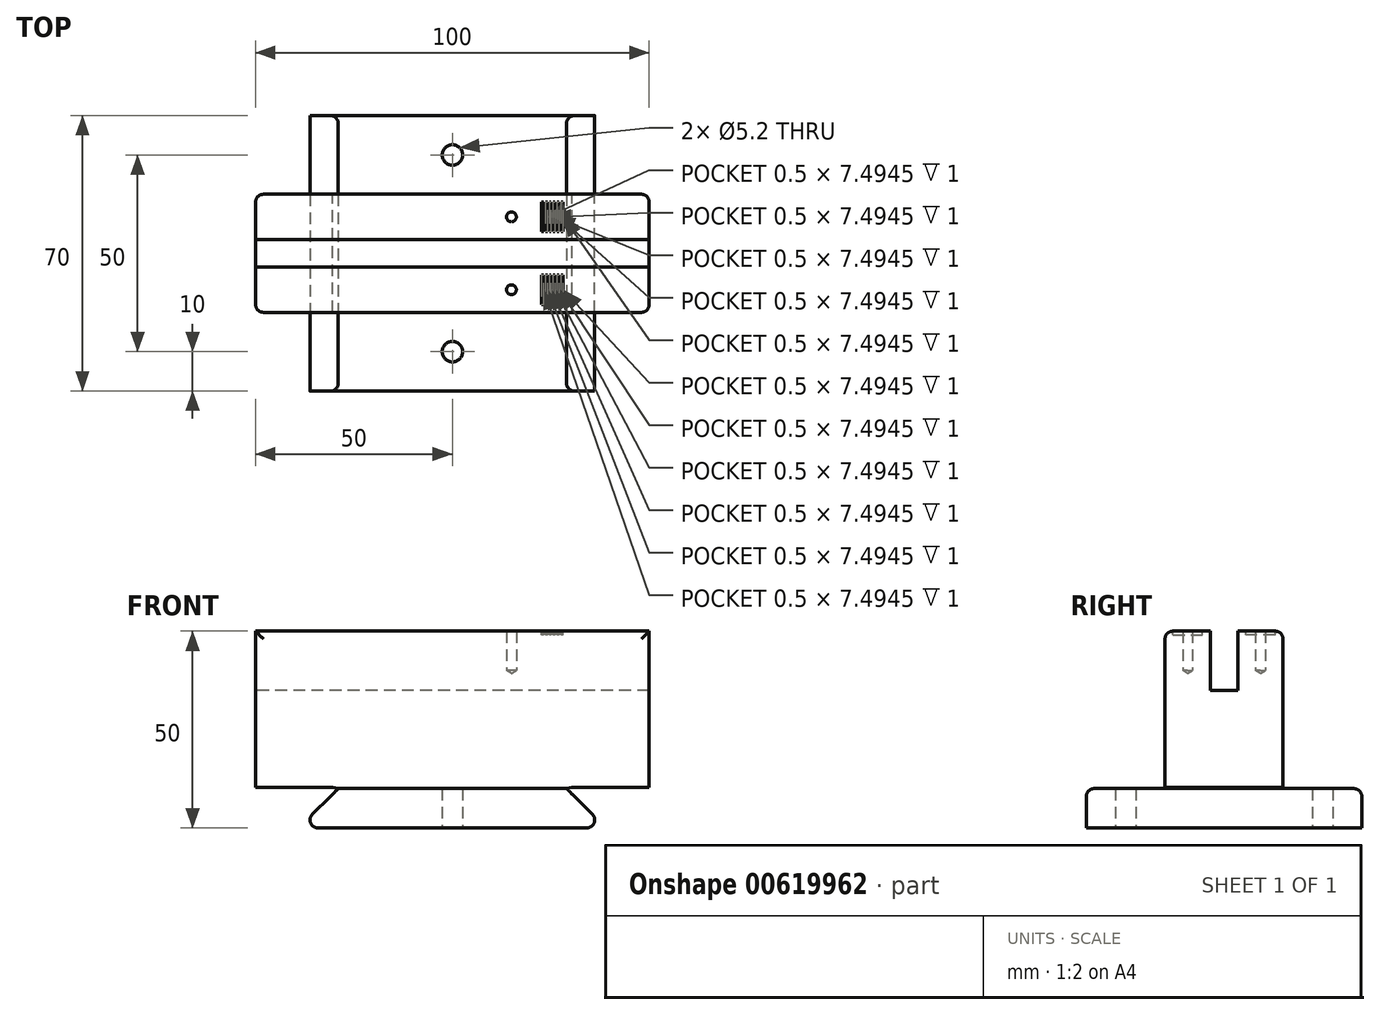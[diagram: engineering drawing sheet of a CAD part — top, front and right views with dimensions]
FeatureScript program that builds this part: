
annotation { "Feature Type Name" : "Feature", "Feature Type Description" : "" }
export const myFeature = defineFeature(function(context is Context, id is Id, definition is map)
    precondition{}
    {
        {
            var Q0;
            Q0=qCreatedBy(makeId("Top.planeOp"),FACE);
            var sketch = newSketch(context, id + "F0", { "sketchPlane" : qUnion([Q0])});
            skLineSegment(sketch, "E0.bottom", {"start": v(39, 35) * mm, "end": v(-39, 35) * mm});
            skLineSegment(sketch, "E0.top", {"start": v(39, -35) * mm, "end": v(-39, -35) * mm});
            skLineSegment(sketch, "E0.left", {"start": v(39, 35) * mm, "end": v(39, -35) * mm});
            skLineSegment(sketch, "E0.right", {"start": v(-39, 35) * mm, "end": v(-39, -35) * mm});
            skPoint(sketch, "E0.middle", {"position": v(0, 0) * mm});
            skSolve(sketch);
        }
        {
            var Q0;
            Q0 = qSketchRegion(id + "F0", true);
            extrude(context, id + "F1", {"entities" : qUnion([Q0]), "depth" : 10 * mm, "offsetDistance" : 25 * mm});
        }
        {
            var Q0;
            Q0=makeQuery(id+"F1.opExtrude","SWEPT_FACE",FACE,{"disambiguationData":[OSD([sQuery(id+"F0.wireOp",EDGE,"E0.top")])]});
            var sketch = newSketch(context, id + "F2", { "sketchPlane" : qUnion([Q0])});
            skLineSegment(sketch, "E1", {"start": v(-39, 0) * mm, "end": v(-29, 10) * mm});
            skLineSegment(sketch, "E2", {"start": v(0, 0) * mm, "end": v(0, 10) * mm, "construction": true});
            skLineSegment(sketch, "E3.MirrorCS", {"start": v(39, 0) * mm, "end": v(29, 10) * mm});
            skSolve(sketch);
        }
        {
            var Q0;
            Q0 = qSketchRegion(id + "F2", true);
            var Q1;
            {var subQ0=sQuery(id+"F2.wireOp",EDGE,"E1");Q1=makeQuery(id+"F2.imprint","IMPRINT",FACE,{"disambiguationData":[TD([[makeQuery(id+"F2.imprint","IMPRINT",EDGE,{"derivedFrom":subQ0}),1.0]])]});}
            var Q2;
            {var subQ0=sQuery(id+"F2.wireOp",EDGE,"E3.MirrorCS");Q2=makeQuery(id+"F2.imprint","IMPRINT",FACE,{"disambiguationData":[TD([[makeQuery(id+"F2.imprint","IMPRINT",EDGE,{"derivedFrom":subQ0}),-1.0]])]});}
            extrude(context, id + "F3", {"entities" : qUnion([Q0, Q1, Q2]), "operationType" : NewBodyOperationType.REMOVE, "oppositeDirection" : true, "depth" : 70 * mm, "offsetDistance" : 25 * mm});
        }
        {
            var Q0;
            Q0=makeQuery(id+"F1.opExtrude","CAP_FACE",FACE,{"disambiguationData":[OSD([sQuery(id+"F0.wireOp",EDGE,"E0.bottom"),sQuery(id+"F0.wireOp",EDGE,"E0.top"),sQuery(id+"F0.wireOp",EDGE,"E0.left"),sQuery(id+"F0.wireOp",EDGE,"E0.right")])],"isStart":false});
            var sketch = newSketch(context, id + "F4", { "sketchPlane" : qUnion([Q0])});
            skPoint(sketch, "E4", {"position": v(0, 25) * mm});
            skLineSegment(sketch, "E5", {"start": v(-29, 0) * mm, "end": v(29, 0) * mm, "construction": true});
            skPoint(sketch, "E6.MirrorP", {"position": v(0, -25) * mm});
            skSolve(sketch);
        }
        {
            var Q0;
            Q0=sQuery(id+"F4.wireOp",VERTEX,"E4");
            var Q1;
            Q1=sQuery(id+"F4.wireOp",VERTEX,"E6.MirrorP");
            var Q2;
            Q2=makeQuery(id+"F1.opExtrude","SWEPT_BODY",BODY,{"disambiguationData":[OSD([sQuery(id+"F0.wireOp",EDGE,"E0.bottom"),sQuery(id+"F0.wireOp",EDGE,"E0.top"),sQuery(id+"F0.wireOp",EDGE,"E0.left"),sQuery(id+"F0.wireOp",EDGE,"E0.right")])]});
            hole(context, id + "F5", {"style" : HoleStyle.SIMPLE, "endStyle" : HoleEndStyle.THROUGH, "standardTappedOrClearance" : lookupTablePath({ "standard" : "ISO", "size" : "5.2", "type" : "Drilled" }), "standardBlindInLast" : lookupTablePath({ "standard" : "ISO", "size" : "5.2", "type" : "Drilled" }), "holeDiameter" : 5.2 * mm, "majorDiameter" : 5 * mm, "isTappedThrough" : true, "tappedDepth" : 7.6 * mm, "tapClearance" : 3, "locations" : qUnion([Q0, Q1]), "scope" : qUnion([Q2]), "startStyle" : HoleStartStyle.SKETCH});
        }
        {
            var Q0;
            Q0=makeQuery(id+"F1.opExtrude","CAP_FACE",FACE,{"disambiguationData":[OSD([sQuery(id+"F0.wireOp",EDGE,"E0.bottom"),sQuery(id+"F0.wireOp",EDGE,"E0.top"),sQuery(id+"F0.wireOp",EDGE,"E0.left"),sQuery(id+"F0.wireOp",EDGE,"E0.right")])],"isStart":false});
            var sketch = newSketch(context, id + "F6", { "sketchPlane" : qUnion([Q0])});
            skLineSegment(sketch, "E7.bottom", {"start": v(50, 15) * mm, "end": v(-50, 15) * mm});
            skLineSegment(sketch, "E7.top", {"start": v(50, -15) * mm, "end": v(-50, -15) * mm});
            skLineSegment(sketch, "E7.left", {"start": v(50, 15) * mm, "end": v(50, -15) * mm});
            skLineSegment(sketch, "E7.right", {"start": v(-50, 15) * mm, "end": v(-50, -15) * mm});
            skPoint(sketch, "E7.middle", {"position": v(0, 0) * mm});
            skSolve(sketch);
        }
        {
            var Q0;
            Q0 = qSketchRegion(id + "F6", true);
            extrude(context, id + "F7", {"entities" : qUnion([Q0]), "operationType" : NewBodyOperationType.ADD, "depth" : 40 * mm, "offsetDistance" : 25 * mm});
        }
        {
            var Q0;
            Q0=makeQuery(id+"F7.opExtrude","CAP_FACE",FACE,{"disambiguationData":[OSD([sQuery(id+"F6.wireOp",EDGE,"E7.bottom"),sQuery(id+"F6.wireOp",EDGE,"E7.top"),sQuery(id+"F6.wireOp",EDGE,"E7.left"),sQuery(id+"F6.wireOp",EDGE,"E7.right")])],"isStart":false});
            var sketch = newSketch(context, id + "F8", { "sketchPlane" : qUnion([Q0])});
            skLineSegment(sketch, "E8.bottom", {"start": v(50, 3.5) * mm, "end": v(-50, 3.5) * mm});
            skLineSegment(sketch, "E8.top", {"start": v(50, -3.5) * mm, "end": v(-50, -3.5) * mm});
            skLineSegment(sketch, "E8.left", {"start": v(50, 3.5) * mm, "end": v(50, -3.5) * mm});
            skLineSegment(sketch, "E8.right", {"start": v(-50, 3.5) * mm, "end": v(-50, -3.5) * mm});
            skPoint(sketch, "E8.middle", {"position": v(0, 0) * mm});
            skSolve(sketch);
        }
        {
            var Q0;
            Q0=makeQuery(id+"F8.imprint","IMPRINT",FACE,{"disambiguationData":[TD([[makeQuery(id+"F8.imprint","IMPRINT",EDGE,{"derivedFrom":sQuery(id+"F8.wireOp",EDGE,"E8.bottom")}),1.0]])]});
            extrude(context, id + "F9", {"entities" : qUnion([Q0]), "operationType" : NewBodyOperationType.REMOVE, "oppositeDirection" : true, "depth" : 15 * mm, "offsetDistance" : 25 * mm});
        }
        {
            var Q0;
            Q0=makeQuery(id+"F7.opExtrude","SWEPT_FACE",FACE,{"disambiguationData":[OSD([sQuery(id+"F6.wireOp",EDGE,"E7.bottom")])]});
            var sketch = newSketch(context, id + "F10", { "sketchPlane" : qUnion([Q0])});
            skPoint(sketch, "E9", {"position": v(-50, 10.3) * mm});
            skPoint(sketch, "E10", {"position": v(-30.4, 10.3) * mm});
            skLineSegment(sketch, "E11", {"start": v(-29, 10) * mm, "end": v(-30.4, 10.3) * mm});
            skLineSegment(sketch, "E12", {"start": v(-30.4, 10.3) * mm, "end": v(-50, 10.3) * mm});
            skLineSegment(sketch, "E13", {"start": v(0, 0) * mm, "end": v(0, 50) * mm, "construction": true});
            skLineSegment(sketch, "E14.MirrorCS", {"start": v(29, 10) * mm, "end": v(30.4, 10.3) * mm});
            skLineSegment(sketch, "E15.MirrorCS", {"start": v(30.4, 10.3) * mm, "end": v(50, 10.3) * mm});
            skSolve(sketch);
        }
        {
            var Q0;
            Q0=makeQuery(id+"F10.imprint","IMPRINT",FACE,{"disambiguationData":[TD([[makeQuery(id+"F10.imprint","IMPRINT",EDGE,{"derivedFrom":sQuery(id+"F10.wireOp",EDGE,"E11")}),1.0]])]});
            var Q1;
            Q1=makeQuery(id+"F10.imprint","IMPRINT",FACE,{"disambiguationData":[TD([[makeQuery(id+"F10.imprint","IMPRINT",EDGE,{"derivedFrom":sQuery(id+"F10.wireOp",EDGE,"E14.MirrorCS")}),-1.0]])]});
            extrude(context, id + "F11", {"entities" : qUnion([Q0, Q1]), "operationType" : NewBodyOperationType.REMOVE, "endBound" : BoundingType.THROUGH_ALL, "oppositeDirection" : true, "depth" : 25 * mm, "offsetDistance" : 25 * mm});
        }
        {
            var Q0;
            {var subQ1=sQuery(id+"F2.wireOp",EDGE,"E3.MirrorCS");var subQ2=makeQuery(id+"F3.boolean.opBoolean","COPY",FACE,{"derivedFrom":makeQuery(id+"F3.opExtrude","SWEPT_FACE",FACE,{"disambiguationData":[OSD([subQ1])]})});var subQ3=sQuery(id+"F0.wireOp",EDGE,"E0.top");var subQ4=makeQuery(id+"F1.opExtrude","CAP_FACE",FACE,{"disambiguationData":[OSD([sQuery(id+"F0.wireOp",EDGE,"E0.bottom"),subQ3,sQuery(id+"F0.wireOp",EDGE,"E0.left"),sQuery(id+"F0.wireOp",EDGE,"E0.right")])],"isStart":false});Q0=makeQuery(id+"F7.boolean.opBoolean","SPLIT",EDGE,{"disambiguationData":[topologyDisambiguationEdgeConnected([subQ4,subQ2]),TD([makeQuery(id+"F1.opExtrude","SWEPT_FACE",FACE,{"disambiguationData":[OSD([subQ3])]})])],"derivedFrom":makeQuery(id+"F3.boolean.opBoolean","COPY",EDGE,{"derivedFrom":makeQuery(id+"F3.opExtrude","SWEPT_EDGE",EDGE,{"disambiguationData":[OSD([subQ3,subQ1])]})})});}
            var Q1;
            {var subQ0=sQuery(id+"F0.wireOp",EDGE,"E0.top");var subQ1=sQuery(id+"F0.wireOp",EDGE,"E0.bottom");var subQ2=makeQuery(id+"F1.opExtrude","CAP_FACE",FACE,{"disambiguationData":[OSD([subQ1,subQ0,sQuery(id+"F0.wireOp",EDGE,"E0.left"),sQuery(id+"F0.wireOp",EDGE,"E0.right")])],"isStart":false});var subQ4=sQuery(id+"F2.wireOp",EDGE,"E3.MirrorCS");var subQ5=makeQuery(id+"F3.boolean.opBoolean","COPY",FACE,{"derivedFrom":makeQuery(id+"F3.opExtrude","SWEPT_FACE",FACE,{"disambiguationData":[OSD([subQ4])]})});Q1=makeQuery(id+"F7.boolean.opBoolean","SPLIT",EDGE,{"disambiguationData":[topologyDisambiguationEdgeConnected([subQ2,subQ5]),TD([makeQuery(id+"F1.opExtrude","SWEPT_FACE",FACE,{"disambiguationData":[OSD([subQ1])]})])],"derivedFrom":makeQuery(id+"F3.boolean.opBoolean","COPY",EDGE,{"derivedFrom":makeQuery(id+"F3.opExtrude","SWEPT_EDGE",EDGE,{"disambiguationData":[OSD([subQ0,subQ4])]})})});}
            var Q2;
            Q2=makeQuery(id+"F3.boolean.opBoolean","COPY",EDGE,{"derivedFrom":makeQuery(id+"F3.opExtrude","CAP_EDGE",EDGE,{"disambiguationData":[OSD([sQuery(id+"F2.wireOp",EDGE,"E3.MirrorCS")])],"isStart":false})});
            var Q3;
            {var subQ0=sQuery(id+"F0.wireOp",EDGE,"E0.left");Q3=makeQuery(id+"F3.boolean.opBoolean","MERGE",EDGE,{"derivedFrom":[makeQuery(id+"F1.opExtrude","CAP_EDGE",EDGE,{"disambiguationData":[OSD([subQ0])],"isStart":true}),makeQuery(id+"F3.opExtrude","SWEPT_EDGE",EDGE,{"disambiguationData":[OSD([sQuery(id+"F0.wireOp",EDGE,"E0.top"),subQ0,sQuery(id+"F2.wireOp",EDGE,"E3.MirrorCS")])]})]});}
            var Q4;
            Q4=makeQuery(id+"F3.boolean.opBoolean","COPY",EDGE,{"derivedFrom":makeQuery(id+"F3.opExtrude","CAP_EDGE",EDGE,{"disambiguationData":[OSD([sQuery(id+"F2.wireOp",EDGE,"E3.MirrorCS")])],"isStart":true})});
            var Q5;
            Q5=makeQuery(id+"F1.opExtrude","CAP_EDGE",EDGE,{"disambiguationData":[OSD([sQuery(id+"F0.wireOp",EDGE,"E0.bottom")])],"isStart":false});
            var Q6;
            Q6=makeQuery(id+"F1.opExtrude","CAP_EDGE",EDGE,{"disambiguationData":[OSD([sQuery(id+"F0.wireOp",EDGE,"E0.top")])],"isStart":false});
            var Q7;
            Q7=makeQuery(id+"F7.opExtrude","CAP_EDGE",EDGE,{"disambiguationData":[OSD([sQuery(id+"F6.wireOp",EDGE,"E7.top")])],"isStart":false});
            var Q8;
            Q8=makeQuery(id+"F9.boolean.opBoolean","COPY",EDGE,{"derivedFrom":makeQuery(id+"F9.opExtrude","CAP_EDGE",EDGE,{"disambiguationData":[OSD([sQuery(id+"F8.wireOp",EDGE,"E8.top")])],"isStart":true})});
            var Q9;
            Q9=makeQuery(id+"F9.boolean.opBoolean","COPY",EDGE,{"derivedFrom":makeQuery(id+"F9.opExtrude","CAP_EDGE",EDGE,{"disambiguationData":[OSD([sQuery(id+"F8.wireOp",EDGE,"E8.bottom")])],"isStart":true})});
            var Q10;
            Q10=makeQuery(id+"F7.opExtrude","CAP_EDGE",EDGE,{"disambiguationData":[OSD([sQuery(id+"F6.wireOp",EDGE,"E7.bottom")])],"isStart":false});
            var Q11;
            Q11=makeQuery(id+"F7.opExtrude","SWEPT_EDGE",EDGE,{"disambiguationData":[OSD([sQuery(id+"F6.wireOp",EDGE,"E7.bottom"),sQuery(id+"F6.wireOp",EDGE,"E7.left")])]});
            var Q12;
            Q12=makeQuery(id+"F7.opExtrude","SWEPT_EDGE",EDGE,{"disambiguationData":[OSD([sQuery(id+"F6.wireOp",EDGE,"E7.top"),sQuery(id+"F6.wireOp",EDGE,"E7.left")])]});
            var Q13;
            Q13=makeQuery(id+"F11.boolean.opBoolean","COPY",EDGE,{"derivedFrom":makeQuery(id+"F11.opExtrude","SWEPT_EDGE",EDGE,{"disambiguationData":[OSD([sQuery(id+"F6.wireOp",EDGE,"E7.bottom"),sQuery(id+"F6.wireOp",EDGE,"E7.left"),sQuery(id+"F10.wireOp",EDGE,"E12")])]})});
            var Q14;
            {var subQ1=sQuery(id+"F2.wireOp",EDGE,"E1");var subQ2=makeQuery(id+"F3.boolean.opBoolean","COPY",FACE,{"derivedFrom":makeQuery(id+"F3.opExtrude","SWEPT_FACE",FACE,{"disambiguationData":[OSD([subQ1])]})});var subQ3=sQuery(id+"F0.wireOp",EDGE,"E0.top");var subQ4=makeQuery(id+"F1.opExtrude","CAP_FACE",FACE,{"disambiguationData":[OSD([sQuery(id+"F0.wireOp",EDGE,"E0.bottom"),subQ3,sQuery(id+"F0.wireOp",EDGE,"E0.left"),sQuery(id+"F0.wireOp",EDGE,"E0.right")])],"isStart":false});Q14=makeQuery(id+"F7.boolean.opBoolean","SPLIT",EDGE,{"disambiguationData":[topologyDisambiguationEdgeConnected([subQ4,subQ2]),TD([makeQuery(id+"F1.opExtrude","SWEPT_FACE",FACE,{"disambiguationData":[OSD([subQ3])]})])],"derivedFrom":makeQuery(id+"F3.boolean.opBoolean","COPY",EDGE,{"derivedFrom":makeQuery(id+"F3.opExtrude","SWEPT_EDGE",EDGE,{"disambiguationData":[OSD([subQ3,subQ1])]})})});}
            var Q15;
            Q15=makeQuery(id+"F7.opExtrude","SWEPT_EDGE",EDGE,{"disambiguationData":[OSD([sQuery(id+"F6.wireOp",EDGE,"E7.top"),sQuery(id+"F6.wireOp",EDGE,"E7.right")])]});
            var Q16;
            Q16=makeQuery(id+"F7.opExtrude","SWEPT_EDGE",EDGE,{"disambiguationData":[OSD([sQuery(id+"F6.wireOp",EDGE,"E7.bottom"),sQuery(id+"F6.wireOp",EDGE,"E7.right")])]});
            var Q17;
            Q17=makeQuery(id+"F11.boolean.opBoolean","COPY",EDGE,{"derivedFrom":makeQuery(id+"F11.opExtrude","SWEPT_EDGE",EDGE,{"disambiguationData":[OSD([sQuery(id+"F6.wireOp",EDGE,"E7.bottom"),sQuery(id+"F6.wireOp",EDGE,"E7.right"),sQuery(id+"F10.wireOp",EDGE,"E15.MirrorCS")])]})});
            var Q18;
            {var subQ0=sQuery(id+"F0.wireOp",EDGE,"E0.right");Q18=makeQuery(id+"F3.boolean.opBoolean","MERGE",EDGE,{"derivedFrom":[makeQuery(id+"F1.opExtrude","CAP_EDGE",EDGE,{"disambiguationData":[OSD([subQ0])],"isStart":true}),makeQuery(id+"F3.opExtrude","SWEPT_EDGE",EDGE,{"disambiguationData":[OSD([sQuery(id+"F0.wireOp",EDGE,"E0.top"),subQ0,sQuery(id+"F2.wireOp",EDGE,"E1")])]})]});}
            var Q19;
            Q19=makeQuery(id+"F3.boolean.opBoolean","COPY",EDGE,{"derivedFrom":makeQuery(id+"F3.opExtrude","CAP_EDGE",EDGE,{"disambiguationData":[OSD([sQuery(id+"F2.wireOp",EDGE,"E1")])],"isStart":true})});
            var Q20;
            Q20=makeQuery(id+"F3.boolean.opBoolean","COPY",EDGE,{"derivedFrom":makeQuery(id+"F3.opExtrude","CAP_EDGE",EDGE,{"disambiguationData":[OSD([sQuery(id+"F2.wireOp",EDGE,"E1")])],"isStart":false})});
            fillet(context, id + "F12", {"entities" : qUnion([Q0, Q1, Q2, Q3, Q4, Q5, Q6, Q7, Q8, Q9, Q10, Q11, Q12, Q13, Q14, Q15, Q16, Q17, Q18, Q19, Q20]), "radius" : 2 * mm, "tangentPropagation" : true, "defaultsChanged" : false, "vertexSettings" : [], "allowEdgeOverflow" : false});
        }
        {
            var Q0;
            {var subQ0=sQuery(id+"F6.wireOp",EDGE,"E7.bottom");var subQ1=sQuery(id+"F6.wireOp",EDGE,"E7.right");var subQ2=sQuery(id+"F6.wireOp",EDGE,"E7.left");Q0=makeQuery(id+"F9.boolean.opBoolean","SPLIT",FACE,{"disambiguationData":[TD([makeQuery(id+"F7.opExtrude","SWEPT_FACE",FACE,{"disambiguationData":[OSD([subQ0])]})])],"derivedFrom":makeQuery(id+"F7.opExtrude","CAP_FACE",FACE,{"disambiguationData":[OSD([subQ0,sQuery(id+"F6.wireOp",EDGE,"E7.top"),subQ2,subQ1])],"isStart":false})});}
            var sketch = newSketch(context, id + "F13", { "sketchPlane" : qUnion([Q0])});
            skPoint(sketch, "E16", {"position": v(15, 9.25) * mm});
            skLineSegment(sketch, "E17", {"start": v(28.38, 13) * mm, "end": v(28.38, 5.5) * mm, "construction": true});
            skPoint(sketch, "E18", {"position": v(27.88, 9.25) * mm});
            skLineSegment(sketch, "E19.bottom", {"start": v(27.63, 13) * mm, "end": v(28.13, 13) * mm});
            skLineSegment(sketch, "E19.top", {"start": v(27.63, 5.5) * mm, "end": v(28.13, 5.5) * mm});
            skLineSegment(sketch, "E19.left", {"start": v(27.63, 13) * mm, "end": v(27.63, 5.5) * mm});
            skLineSegment(sketch, "E19.right", {"start": v(28.13, 13) * mm, "end": v(28.13, 5.5) * mm});
            skPoint(sketch, "E20.1.0.0", {"position": v(26.88, 9.25) * mm});
            skLineSegment(sketch, "E20.1.0.1", {"start": v(26.63, 13) * mm, "end": v(27.13, 13) * mm});
            skLineSegment(sketch, "E20.1.0.2", {"start": v(26.63, 5.5) * mm, "end": v(27.13, 5.5) * mm});
            skLineSegment(sketch, "E20.1.0.3", {"start": v(26.63, 13) * mm, "end": v(26.63, 5.5) * mm});
            skLineSegment(sketch, "E20.1.0.4", {"start": v(27.13, 13) * mm, "end": v(27.13, 5.5) * mm});
            skPoint(sketch, "E20.1.0.5", {"position": v(26.88, 9.25) * mm});
            skPoint(sketch, "E20.2.0.0", {"position": v(25.88, 9.25) * mm});
            skLineSegment(sketch, "E20.2.0.1", {"start": v(25.63, 13) * mm, "end": v(26.13, 13) * mm});
            skLineSegment(sketch, "E20.2.0.2", {"start": v(25.63, 5.5) * mm, "end": v(26.13, 5.5) * mm});
            skLineSegment(sketch, "E20.2.0.3", {"start": v(25.63, 13) * mm, "end": v(25.63, 5.5) * mm});
            skLineSegment(sketch, "E20.2.0.4", {"start": v(26.13, 13) * mm, "end": v(26.13, 5.5) * mm});
            skPoint(sketch, "E20.2.0.5", {"position": v(25.88, 9.25) * mm});
            skPoint(sketch, "E20.3.0.0", {"position": v(24.88, 9.25) * mm});
            skLineSegment(sketch, "E20.3.0.1", {"start": v(24.63, 13) * mm, "end": v(25.13, 13) * mm});
            skLineSegment(sketch, "E20.3.0.2", {"start": v(24.63, 5.5) * mm, "end": v(25.13, 5.5) * mm});
            skLineSegment(sketch, "E20.3.0.3", {"start": v(24.63, 13) * mm, "end": v(24.63, 5.5) * mm});
            skLineSegment(sketch, "E20.3.0.4", {"start": v(25.13, 13) * mm, "end": v(25.13, 5.5) * mm});
            skPoint(sketch, "E20.3.0.5", {"position": v(24.88, 9.25) * mm});
            skPoint(sketch, "E20.4.0.0", {"position": v(23.88, 9.25) * mm});
            skLineSegment(sketch, "E20.4.0.1", {"start": v(23.63, 13) * mm, "end": v(24.13, 13) * mm});
            skLineSegment(sketch, "E20.4.0.2", {"start": v(23.63, 5.5) * mm, "end": v(24.13, 5.5) * mm});
            skLineSegment(sketch, "E20.4.0.3", {"start": v(23.63, 13) * mm, "end": v(23.63, 5.5) * mm});
            skLineSegment(sketch, "E20.4.0.4", {"start": v(24.13, 13) * mm, "end": v(24.13, 5.5) * mm});
            skPoint(sketch, "E20.4.0.5", {"position": v(23.88, 9.25) * mm});
            skPoint(sketch, "E20.5.0.0", {"position": v(22.88, 9.25) * mm});
            skLineSegment(sketch, "E20.5.0.1", {"start": v(22.63, 13) * mm, "end": v(23.13, 13) * mm});
            skLineSegment(sketch, "E20.5.0.2", {"start": v(22.63, 5.5) * mm, "end": v(23.13, 5.5) * mm});
            skLineSegment(sketch, "E20.5.0.3", {"start": v(22.63, 13) * mm, "end": v(22.63, 5.5) * mm});
            skLineSegment(sketch, "E20.5.0.4", {"start": v(23.13, 13) * mm, "end": v(23.13, 5.5) * mm});
            skPoint(sketch, "E20.5.0.5", {"position": v(22.88, 9.25) * mm});
            skLineSegment(sketch, "E20.direction1", {"start": v(27.63, 5.5) * mm, "end": v(26.63, 5.5) * mm, "construction": true});
            skLineSegment(sketch, "E21", {"start": v(0, 0) * mm, "end": v(50.09, 0) * mm, "construction": true});
            skLineSegment(sketch, "E22.MirrorCS", {"start": v(28.38, -13) * mm, "end": v(28.38, -5.5) * mm, "construction": true});
            skLineSegment(sketch, "E23.MirrorCS", {"start": v(28.13, -13) * mm, "end": v(28.13, -5.5) * mm});
            skPoint(sketch, "E24.MirrorP", {"position": v(27.88, -9.25) * mm});
            skLineSegment(sketch, "E25.MirrorCS", {"start": v(27.63, -13) * mm, "end": v(27.63, -5.5) * mm});
            skLineSegment(sketch, "E26.MirrorCS", {"start": v(27.13, -13) * mm, "end": v(27.13, -5.5) * mm});
            skPoint(sketch, "E27.MirrorP", {"position": v(26.88, -9.25) * mm});
            skLineSegment(sketch, "E28.MirrorCS", {"start": v(26.63, -13) * mm, "end": v(26.63, -5.5) * mm});
            skLineSegment(sketch, "E29.MirrorCS", {"start": v(26.13, -13) * mm, "end": v(26.13, -5.5) * mm});
            skPoint(sketch, "E30.MirrorP", {"position": v(25.88, -9.25) * mm});
            skLineSegment(sketch, "E31.MirrorCS", {"start": v(25.63, -13) * mm, "end": v(25.63, -5.5) * mm});
            skLineSegment(sketch, "E32.MirrorCS", {"start": v(25.13, -13) * mm, "end": v(25.13, -5.5) * mm});
            skPoint(sketch, "E33.MirrorP", {"position": v(24.88, -9.25) * mm});
            skLineSegment(sketch, "E34.MirrorCS", {"start": v(24.63, -13) * mm, "end": v(24.63, -5.5) * mm});
            skLineSegment(sketch, "E35.MirrorCS", {"start": v(24.13, -13) * mm, "end": v(24.13, -5.5) * mm});
            skPoint(sketch, "E36.MirrorP", {"position": v(23.88, -9.25) * mm});
            skLineSegment(sketch, "E37.MirrorCS", {"start": v(23.63, -13) * mm, "end": v(23.63, -5.5) * mm});
            skLineSegment(sketch, "E38.MirrorCS", {"start": v(23.13, -13) * mm, "end": v(23.13, -5.5) * mm});
            skPoint(sketch, "E39.MirrorP", {"position": v(22.88, -9.25) * mm});
            skLineSegment(sketch, "E40.MirrorCS", {"start": v(22.63, -13) * mm, "end": v(22.63, -5.5) * mm});
            skPoint(sketch, "E41.MirrorP", {"position": v(15, -9.25) * mm});
            skLineSegment(sketch, "E42.MirrorCS", {"start": v(27.63, -13) * mm, "end": v(28.13, -13) * mm});
            skLineSegment(sketch, "E43.MirrorCS", {"start": v(27.63, -5.5) * mm, "end": v(28.13, -5.5) * mm});
            skLineSegment(sketch, "E44.MirrorCS", {"start": v(26.63, -13) * mm, "end": v(27.13, -13) * mm});
            skLineSegment(sketch, "E45.MirrorCS", {"start": v(27.63, -5.5) * mm, "end": v(26.63, -5.5) * mm, "construction": true});
            skLineSegment(sketch, "E46.MirrorCS", {"start": v(25.63, -5.5) * mm, "end": v(26.13, -5.5) * mm});
            skLineSegment(sketch, "E47.MirrorCS", {"start": v(25.63, -13) * mm, "end": v(26.13, -13) * mm});
            skLineSegment(sketch, "E48.MirrorCS", {"start": v(24.63, -13) * mm, "end": v(25.13, -13) * mm});
            skLineSegment(sketch, "E49.MirrorCS", {"start": v(24.63, -5.5) * mm, "end": v(25.13, -5.5) * mm});
            skLineSegment(sketch, "E50.MirrorCS", {"start": v(23.63, -13) * mm, "end": v(24.13, -13) * mm});
            skLineSegment(sketch, "E51.MirrorCS", {"start": v(23.63, -5.5) * mm, "end": v(24.13, -5.5) * mm});
            skLineSegment(sketch, "E52.MirrorCS", {"start": v(22.63, -13) * mm, "end": v(23.13, -13) * mm});
            skLineSegment(sketch, "E53.MirrorCS", {"start": v(22.63, -5.5) * mm, "end": v(23.13, -5.5) * mm});
            skLineSegment(sketch, "E54.MirrorCS", {"start": v(26.63, -5.5) * mm, "end": v(27.13, -5.5) * mm});
            skSolve(sketch);
        }
        {
            var Q0;
            Q0 = qSketchRegion(id + "F13", true);
            extrude(context, id + "F14", {"entities" : qUnion([Q0]), "operationType" : NewBodyOperationType.REMOVE, "oppositeDirection" : true, "depth" : 1 * mm, "offsetDistance" : 25 * mm});
        }
        {
            var Q0;
            Q0=sQuery(id+"F13.wireOp",VERTEX,"E16");
            var Q1;
            Q1=sQuery(id+"F13.wireOp",VERTEX,"E41.MirrorP");
            var Q2;
            Q2=makeQuery(id+"F1.opExtrude","SWEPT_BODY",BODY,{"disambiguationData":[OSD([sQuery(id+"F0.wireOp",EDGE,"E0.bottom"),sQuery(id+"F0.wireOp",EDGE,"E0.top"),sQuery(id+"F0.wireOp",EDGE,"E0.left"),sQuery(id+"F0.wireOp",EDGE,"E0.right")])]});
            hole(context, id + "F15", {"style" : HoleStyle.SIMPLE, "endStyle" : HoleEndStyle.BLIND, "standardTappedOrClearance" : lookupTablePath({ "standard" : "ISO", "engagement" : "75%", "pitch" : "0.5 mm", "size" : "M3", "type" : "Tapped" }), "standardBlindInLast" : lookupTablePath({ "standard" : "ISO", "engagement" : "75%", "pitch" : "0.5 mm", "size" : "M3", "type" : "Tapped" }), "holeDiameter" : 2.5 * mm, "majorDiameter" : 3 * mm, "showTappedDepth" : true, "holeDepth" : 10 * mm, "isTappedThrough" : true, "tappedDepth" : 10 * mm, "tapClearance" : 0, "locations" : qUnion([Q0, Q1]), "scope" : qUnion([Q2]), "startStyle" : HoleStartStyle.SKETCH});
        }
    });
